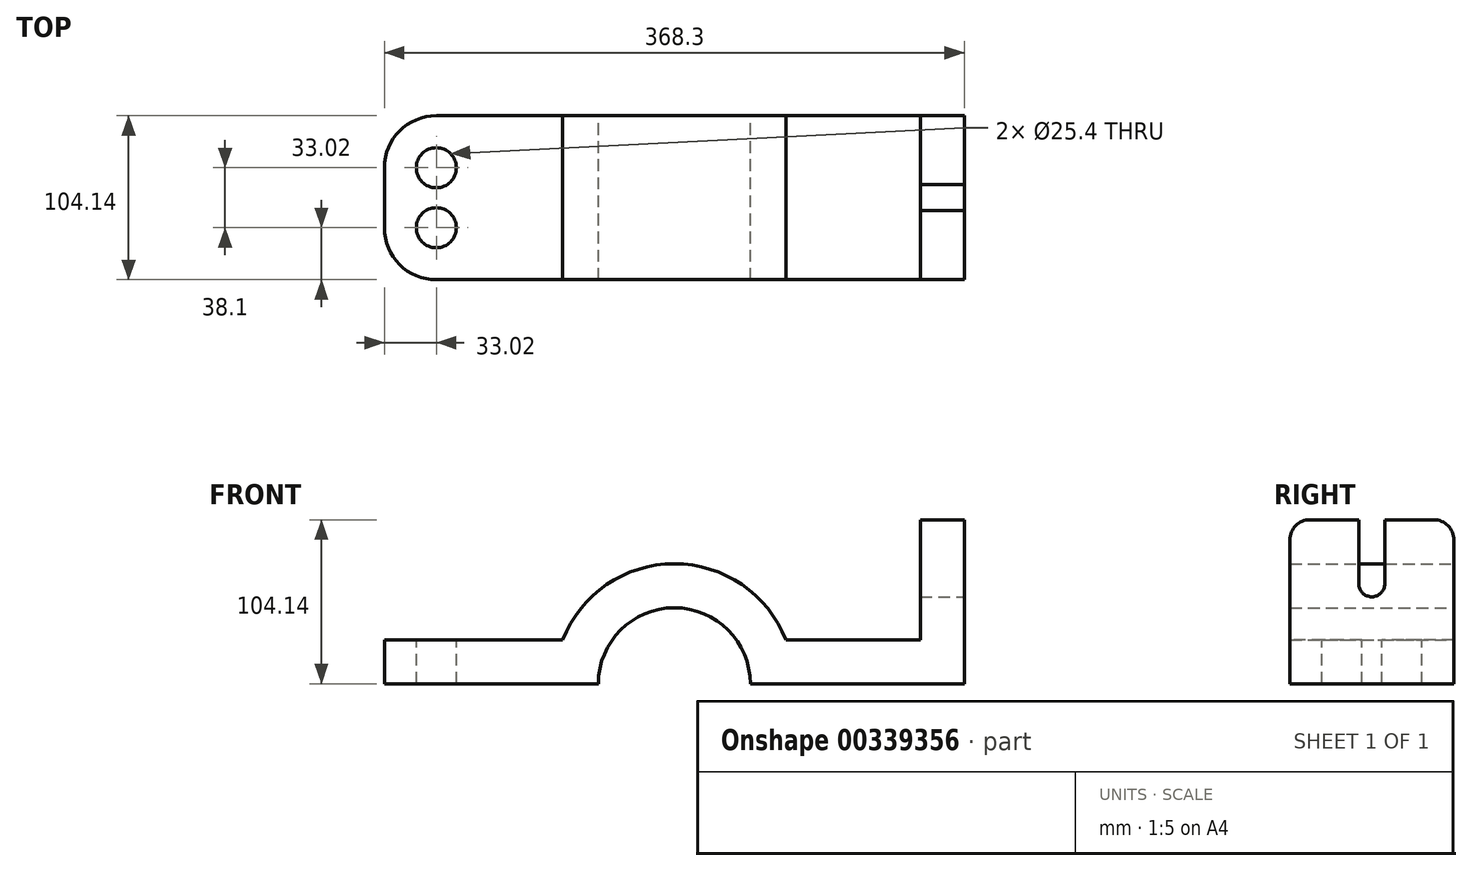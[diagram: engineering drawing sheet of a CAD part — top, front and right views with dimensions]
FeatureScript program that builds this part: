
annotation { "Feature Type Name" : "Feature", "Feature Type Description" : "" }
export const myFeature = defineFeature(function(context is Context, id is Id, definition is map)
    precondition{}
    {
        {
            var Q0;
            Q0=qCreatedBy(makeId("Front.planeOp"),FACE);
            var sketch = newSketch(context, id + "F0", { "sketchPlane" : qUnion([Q0])});
            skLineSegment(sketch, "E0", {"start": v(0, 142.52) * mm, "end": v(0, -100.12) * mm, "construction": true});
            skLineSegment(sketch, "E1", {"start": v(-184.15, 0) * mm, "end": v(-48.26, 0) * mm});
            skLineSegment(sketch, "E2", {"start": v(67.88, 0) * mm, "end": v(67.88, 0) * mm});
            skArc(sketch, "E3", {"start": v(0, 48.26) * mm, "mid": v(-34.12, 34.12) * mm, "end": v(-48.26, 0) * mm});
            skLineSegment(sketch, "E4.MirrorCS", {"start": v(184.15, 0) * mm, "end": v(48.26, 0) * mm});
            skArc(sketch, "E5.MirrorCS", {"start": v(0, 48.26) * mm, "mid": v(34.12, 34.12) * mm, "end": v(48.26, 0) * mm});
            skLineSegment(sketch, "E6.0", {"start": v(156.21, 27.94) * mm, "end": v(70.9, 27.94) * mm});
            skArc(sketch, "E6.1", {"start": v(0, 76.2) * mm, "mid": v(42.88, 62.99) * mm, "end": v(70.9, 27.94) * mm});
            skArc(sketch, "E6.2", {"start": v(0, 76.2) * mm, "mid": v(-42.88, 62.99) * mm, "end": v(-70.9, 27.94) * mm});
            skLineSegment(sketch, "E6.3", {"start": v(-184.15, 27.94) * mm, "end": v(-70.9, 27.94) * mm});
            skLineSegment(sketch, "E7", {"start": v(-184.15, 0) * mm, "end": v(-184.15, 27.94) * mm});
            skLineSegment(sketch, "E8", {"start": v(184.15, 0) * mm, "end": v(184.15, 104.14) * mm});
            skLineSegment(sketch, "E9", {"start": v(184.15, 104.14) * mm, "end": v(156.21, 104.14) * mm});
            skLineSegment(sketch, "E10", {"start": v(156.21, 104.14) * mm, "end": v(156.21, 27.94) * mm});
            skSolve(sketch);
        }
        {
            var Q0;
            Q0=makeQuery(id+"F0.imprint","IMPRINT",FACE,{"disambiguationData":[TD([[makeQuery(id+"F0.imprint","IMPRINT",EDGE,{"derivedFrom":sQuery(id+"F0.wireOp",EDGE,"E1")}),1.0]])]});
            extrude(context, id + "F1", {"entities" : qUnion([Q0]), "endBound" : BoundingType.SYMMETRIC, "depth" : 104.14 * mm});
        }
        {
            var Q0;
            Q0=makeQuery(id+"F1.opExtrude","CAP_EDGE",EDGE,{"disambiguationData":[OSD([sQuery(id+"F0.wireOp",EDGE,"E7")])],"isStart":true});
            var Q1;
            Q1=makeQuery(id+"F1.opExtrude","CAP_EDGE",EDGE,{"disambiguationData":[OSD([sQuery(id+"F0.wireOp",EDGE,"E7")])],"isStart":false});
            fillet(context, id + "F2", {"entities" : qUnion([Q0, Q1]), "radius" : 33.02 * mm, "tangentPropagation" : true, "allowEdgeOverflow" : false});
        }
        {
            var Q0;
            Q0=makeQuery(id+"F1.opExtrude","SWEPT_FACE",FACE,{"disambiguationData":[OSD([sQuery(id+"F0.wireOp",EDGE,"E6.3")])]});
            var sketch = newSketch(context, id + "F3", { "sketchPlane" : qUnion([Q0])});
            skCircle(sketch, "E11", {"center": v(-151.13, 19.05) * mm, "radius": 12.7 * mm});
            skCircle(sketch, "E12", {"center": v(-151.13, -19.05) * mm, "radius": 12.7 * mm});
            skSolve(sketch);
        }
        {
            var Q0;
            Q0 = qSketchRegion(id + "F3", true);
            extrude(context, id + "F4", {"entities" : qUnion([Q0]), "operationType" : NewBodyOperationType.REMOVE, "oppositeDirection" : true, "depth" : 27.94 * mm});
        }
        {
            var Q0;
            Q0=makeQuery(id+"F1.opExtrude","SWEPT_FACE",FACE,{"disambiguationData":[OSD([sQuery(id+"F0.wireOp",EDGE,"E8")])]});
            var sketch = newSketch(context, id + "F5", { "sketchPlane" : qUnion([Q0])});
            skArc(sketch, "E13", {"start": v(-8.26, 63.5) * mm, "mid": v(0, 55.24) * mm, "end": v(8.26, 63.5) * mm});
            skLineSegment(sketch, "E14", {"start": v(8.26, 63.5) * mm, "end": v(8.25, 104.14) * mm});
            skLineSegment(sketch, "E15", {"start": v(-8.26, 63.5) * mm, "end": v(-8.26, 104.14) * mm});
            skSolve(sketch);
        }
        {
            var Q0;
            Q0=makeQuery(id+"F5.imprint","IMPRINT",FACE,{"disambiguationData":[TD([[makeQuery(id+"F5.imprint","IMPRINT",EDGE,{"derivedFrom":sQuery(id+"F5.wireOp",EDGE,"E13")}),1.0]])]});
            extrude(context, id + "F6", {"entities" : qUnion([Q0]), "operationType" : NewBodyOperationType.REMOVE, "oppositeDirection" : true, "depth" : 27.94 * mm});
        }
        {
            var Q0;
            Q0=makeQuery(id+"F1.opExtrude","CAP_EDGE",EDGE,{"disambiguationData":[OSD([sQuery(id+"F0.wireOp",EDGE,"E9")])],"isStart":false});
            var Q1;
            Q1=makeQuery(id+"F1.opExtrude","CAP_EDGE",EDGE,{"disambiguationData":[OSD([sQuery(id+"F0.wireOp",EDGE,"E9")])],"isStart":true});
            fillet(context, id + "F7", {"entities" : qUnion([Q0, Q1]), "radius" : 12.7 * mm, "tangentPropagation" : true, "allowEdgeOverflow" : false});
        }
    });
